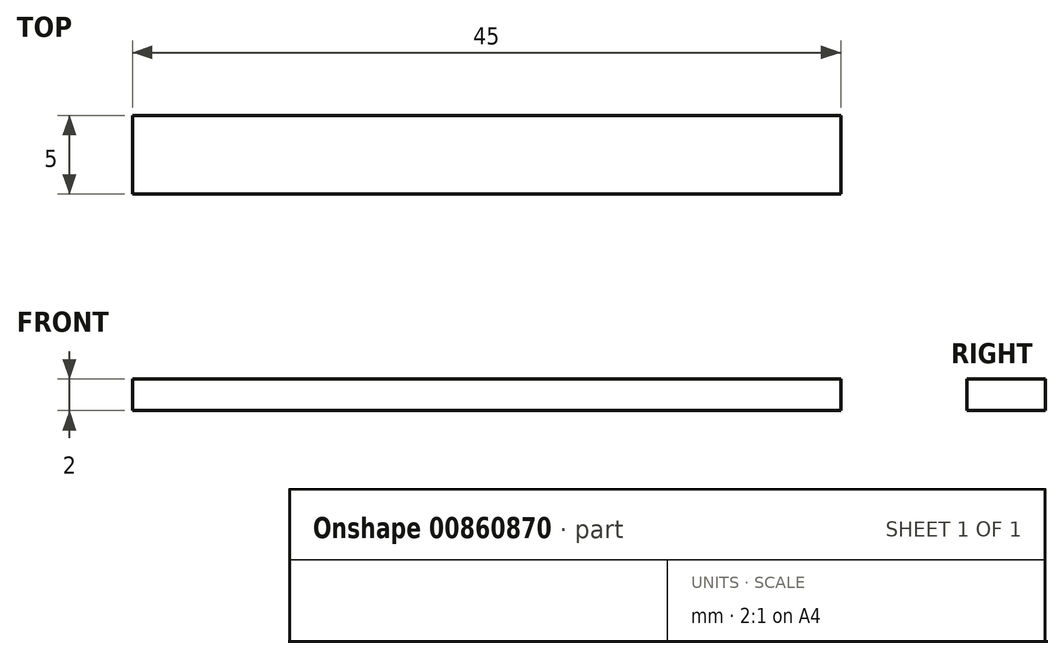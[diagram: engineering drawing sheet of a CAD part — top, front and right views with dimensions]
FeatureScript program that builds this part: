
annotation { "Feature Type Name" : "Feature", "Feature Type Description" : "" }
export const myFeature = defineFeature(function(context is Context, id is Id, definition is map)
    precondition{}
    {
        {
            var Q0;
            Q0=qCreatedBy(makeId("Right.planeOp"),FACE);
            var sketch = newSketch(context, id + "F0", { "sketchPlane" : qUnion([Q0])});
            skLineSegment(sketch, "E0.bottom", {"start": v(-7.4, 4.67) * mm, "end": v(-12.4, 4.67) * mm});
            skLineSegment(sketch, "E0.top", {"start": v(-7.4, 6.67) * mm, "end": v(-12.4, 6.67) * mm});
            skLineSegment(sketch, "E0.left", {"start": v(-7.4, 4.67) * mm, "end": v(-7.4, 6.67) * mm});
            skLineSegment(sketch, "E0.right", {"start": v(-12.4, 4.67) * mm, "end": v(-12.4, 6.67) * mm});
            skSolve(sketch);
        }
        {
            var Q0;
            Q0 = qSketchRegion(id + "F0", true);
            extrude(context, id + "F1", {"entities" : qUnion([Q0]), "depth" : 45 * mm, "offsetDistance" : 25 * mm});
        }
    });
